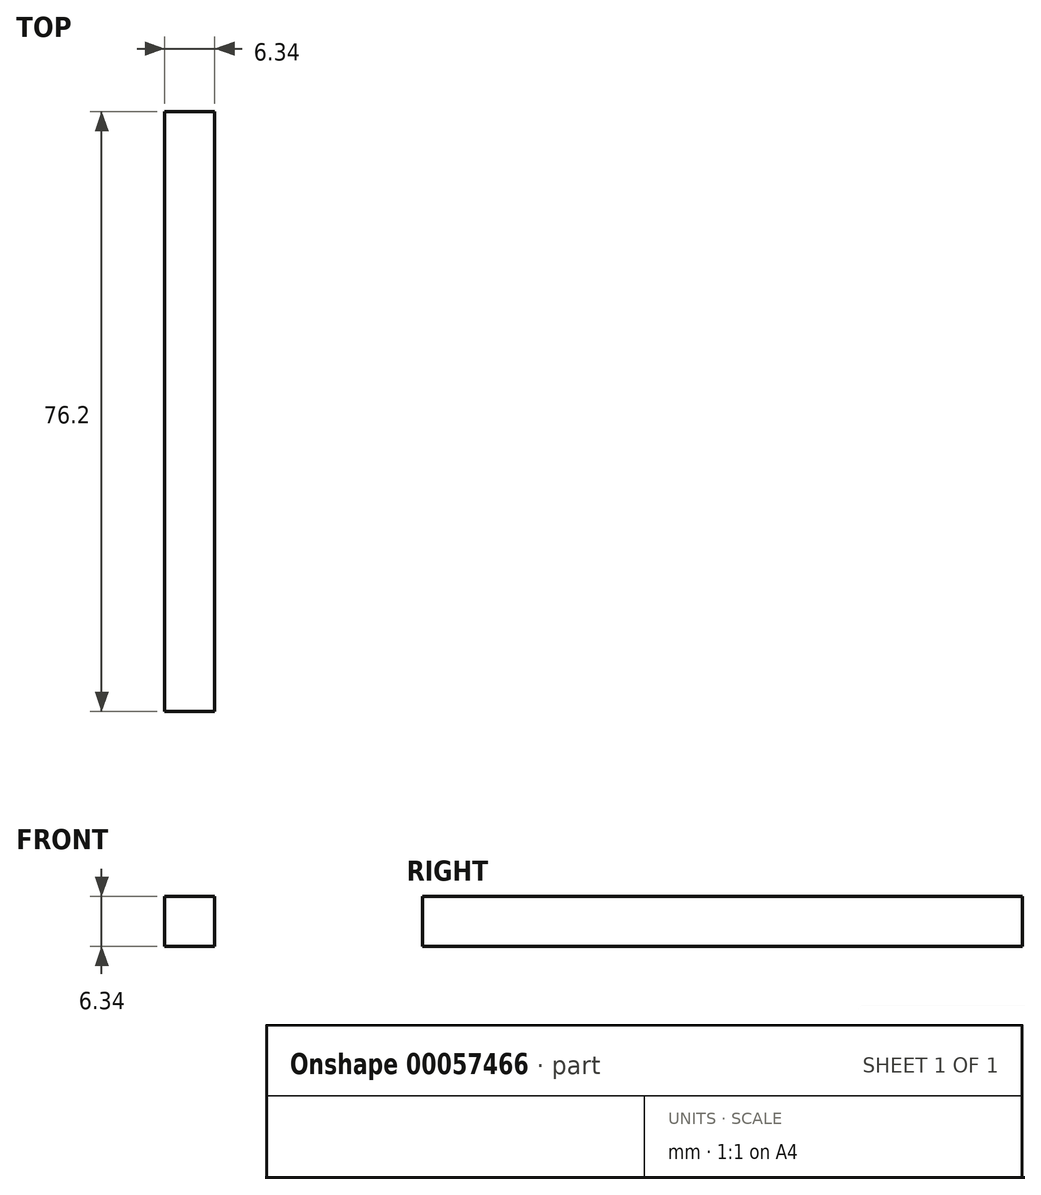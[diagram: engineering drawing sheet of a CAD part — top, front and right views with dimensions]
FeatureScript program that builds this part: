
annotation { "Feature Type Name" : "Feature", "Feature Type Description" : "" }
export const myFeature = defineFeature(function(context is Context, id is Id, definition is map)
    precondition{}
    {
        {
            var Q0;
            Q0=qCreatedBy(makeId("Front.planeOp"),FACE);
            var sketch = newSketch(context, id + "F0", { "sketchPlane" : qUnion([Q0])});
            skLineSegment(sketch, "E0.rect.bottom", {"start": v(3.18, 3.18) * mm, "end": v(-3.18, 3.18) * mm});
            skLineSegment(sketch, "E0.rect.top", {"start": v(3.18, -3.18) * mm, "end": v(-3.18, -3.18) * mm});
            skLineSegment(sketch, "E0.rect.left", {"start": v(3.18, 3.18) * mm, "end": v(3.18, -3.17) * mm});
            skLineSegment(sketch, "E0.rect.right", {"start": v(-3.18, 3.18) * mm, "end": v(-3.18, -3.18) * mm});
            skPoint(sketch, "E0.rect.middle", {"position": v(0, 0) * mm});
            skSolve(sketch);
        }
        {
            var Q0;
            Q0=qSketchRegion(id+"F0",true);
            extrude(context, id + "F1", {"entities" : qUnion([Q0]), "depth" : 76.2 * mm});
        }
    });
